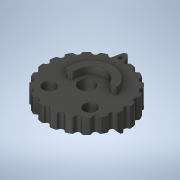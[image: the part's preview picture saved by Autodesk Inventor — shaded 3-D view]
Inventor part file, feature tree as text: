
AUTODESK INVENTOR PART (.ipt)
format: ipt  version: 2020.1 (Build 241239000, 239)  size: 408,064 bytes
history: native  units: mm
features: extrude x8, sketch x4, fillet x2, chamfer x1
ambient origin geometry x8: Origin, YZ Plane, XZ Plane, XY Plane, X Axis, Y Axis, Z Axis, Center Point
bodies: Solid1 (feature_tree)
feature tree (15):
  extrude  "Extrusion1"  Depth=1.25mm
  fillet  "Fillet1"  Radius=8.0mm
  sketch  "Sketch2"  dims[d10=6.3mm d11=12.0mm]
  extrude  "Extrusion2"  Depth=12.0mm
  extrude  "Extrusion3"  Depth=2.0mm TaperAngle=0.0deg
  chamfer  "Chamfer1"  Distance=2.0mm
  extrude  "Extrusion4"  TaperAngle=15.0deg  [1 undecoded]
  extrude  "Extrusion5"  Depth=0.25mm
  extrude  "Extrusion6"  Depth=0.25mm
  extrude  "Extrusion7"  Depth=0.25mm
  extrude  "Extrusion8"  Depth=0.25mm
  fillet  "Fillet2"  Radius=9.0mm
  sketch  "Sketch1"  dims[d1=200.0mm d2=31.0mm d3=360.0deg d6=1.25mm d7=1.25mm d8=8.0mm d9=0.0mm]
  sketch  "Sketch4"  dims[d12=7.0mm d14=2.0mm d15=0.0mm d16=2.0mm d17=0.0mm]
  sketch  "Sketch5"  dims[d18=0.5mm d19=15.0deg d22=5.1mm d23=5.1mm d25=8.726646mm d26=1.5mm d27=9.0mm d28=6.0mm d29=7.330383mm d30=11.5mm d31=11.0mm d32=1.0mm d33=1.5mm d34=1.5mm d35=3.0mm d36=0.0mm d37=5.0mm d38=0.0mm d39=5.0mm d40=0.0mm d41=9.599311mm d43=180.0deg d44=0.0mm d45=2.0mm d46=2.0mm d47=45.0deg d48=1.0mm d49=3.0mm d50=0.0mm d51=0.4mm d52=10.0mm d53=0.0mm d54=0.7mm d55=3.0mm d56=0.0mm d57=0.25mm]
note: 1 required parameter value undecoded (feature->parameter linkage not recoverable at this tier; creation-order binding heuristic only, values carry confidence <= 0.55)
